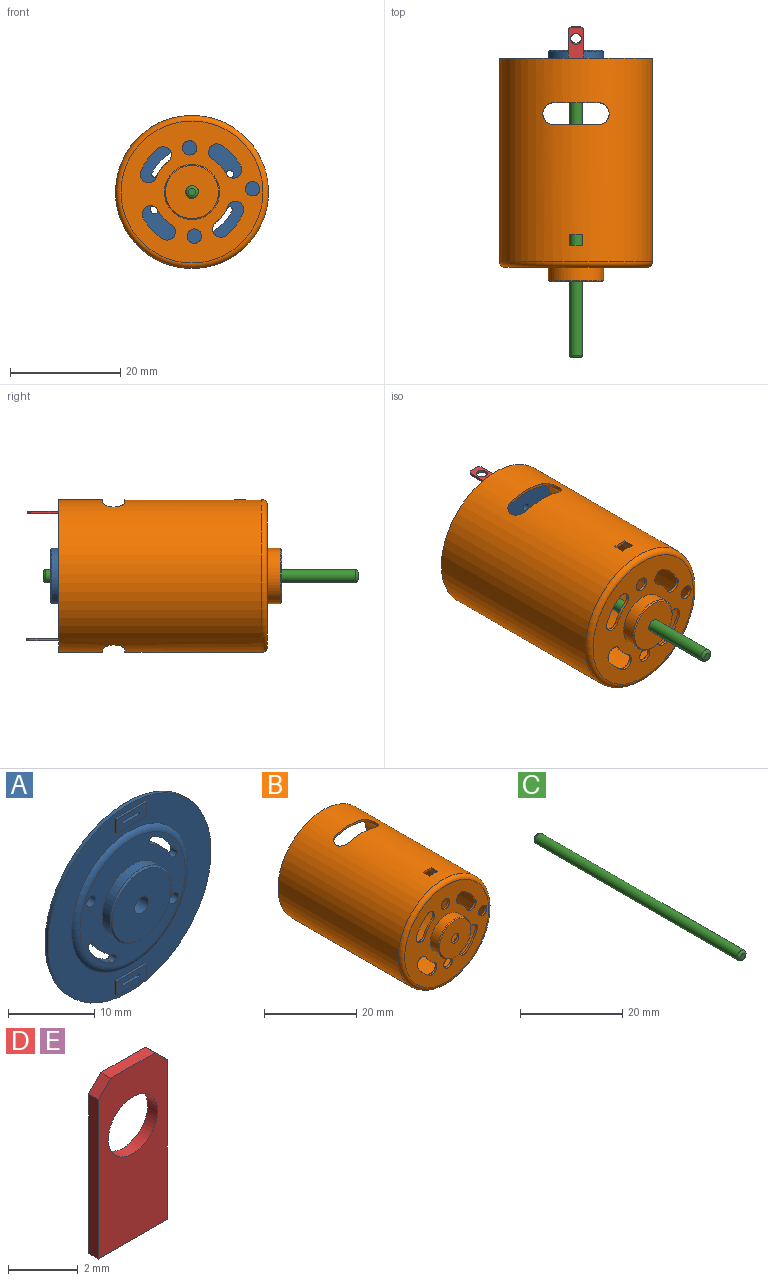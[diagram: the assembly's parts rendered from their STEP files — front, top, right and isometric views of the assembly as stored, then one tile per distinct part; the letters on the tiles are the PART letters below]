
ASSEMBLY  parts=5 mates=4
PART A: 37 faces, bbox 26.7x2.5x26.7 mm
  f0: plane 26.7x26.7mm, normal (0,-1,0), area 256.4mm2, adj f19,f25,f26,f27,f28,f30,f31,f32
  f1: plane 2.8x0.8mm, normal (0,0,-1), area 2.2mm2, adj f2,f20,f21,f29
  f2: plane 0.8x0.4mm, normal (-1,0,0), area 0.3mm2, adj f1,f3,f21,f29
  f3: plane 2.8x0.8mm, normal (0,0,1), area 2.2mm2, adj f2,f20,f21,f29
  f4: cylinder r=8mm len=3.87mm, axis (0,1,0), area 5.6mm2, adj f5,f14,f21,f22
  f5: cylinder r=0.5mm len=1mm, axis (0,1,0), area 1.6mm2, adj f4,f6,f21,f22
  f6: cylinder r=7mm len=3.39mm, axis (0,1,0), area 4.9mm2, adj f5,f14,f21,f22
  f7: cylinder r=0.5mm len=1mm, axis (0,1,0), area 1.6mm2, adj f8,f17,f21,f22
  f8: cylinder r=8mm len=3.87mm, axis (0,1,0), area 5.6mm2, adj f7,f9,f21,f22
  f9: cylinder r=0.5mm len=1mm, axis (0,1,0), area 1.6mm2, adj f8,f17,f21,f22
  f10: plane 2.8x0.8mm, normal (0,0,1), area 2.2mm2, adj f11,f18,f21,f34
  f11: plane 0.8x0.4mm, normal (1,0,0), area 0.3mm2, adj f10,f12,f21,f34
  f12: plane 2.8x0.8mm, normal (0,0,-1), area 2.2mm2, adj f11,f18,f21,f34
  f13: cylinder r=1.15mm len=2.5mm, axis (0,1,0), area 18.1mm2, adj f21,f24
  f14: cylinder r=0.5mm len=1mm, axis (0,1,0), area 1.6mm2, adj f4,f6,f21,f22
  f15: cylinder r=0.75mm len=1.5mm, axis (0,1,0), area 4.7mm2, adj f21,f22
  f16: cylinder r=0.75mm len=1.5mm, axis (0,1,0), area 4.7mm2, adj f21,f22
  f17: cylinder r=7mm len=3.39mm, axis (0,1,0), area 4.9mm2, adj f7,f9,f21,f22
  f18: plane 0.8x0.4mm, normal (-1,0,0), area 0.3mm2, adj f10,f12,f21,f34
  f19: cylinder r=13.35mm len=26.7mm, axis (0,1,0), area 41.9mm2, adj f0,f21
  f20: plane 0.8x0.4mm, normal (1,0,0), area 0.3mm2, adj f1,f3,f21,f29
  f21: plane 26.7x26.7mm, normal (0,1,0), area 537.9mm2, adj f1,f2,f3,f4,f5,f6,f7,f8
  f22: plane 17.27x17.27mm, normal (0,-1,0), area 140.1mm2, adj f4,f5,f6,f7,f8,f9,f14,f15
  f23: cylinder r=5mm len=10mm, axis (0,1,0), area 40.8mm2, adj f22,f36
  f24: plane 9.6x9.6mm, normal (0,-1,0), area 68.2mm2, adj f13,f36
  f25: plane 5x0.3mm, normal (0,0,-1), area 1.5mm2, adj f0,f26,f28,f29
  f26: plane 2x0.3mm, normal (1,0,0), area 0.6mm2, adj f0,f25,f27,f29
  f27: plane 5x0.3mm, normal (0,0,1), area 1.5mm2, adj f0,f26,f28,f29
  f28: plane 2x0.3mm, normal (-1,0,0), area 0.6mm2, adj f0,f25,f27,f29
  f29: plane 5x2mm, normal (0,-1,0), area 8.9mm2, adj f1,f2,f3,f20,f25,f26,f27,f28
  f30: plane 5x0.3mm, normal (0,0,-1), area 1.5mm2, adj f0,f31,f33,f34
  f31: plane 2x0.3mm, normal (1,0,0), area 0.6mm2, adj f0,f30,f32,f34
  f32: plane 5x0.3mm, normal (0,0,1), area 1.5mm2, adj f0,f31,f33,f34
  f33: plane 2x0.3mm, normal (-1,0,0), area 0.6mm2, adj f0,f30,f32,f34
  f34: plane 5x2mm, normal (0,-1,0), area 8.9mm2, adj f10,f11,f12,f18,f30,f31,f32,f33
  f35: torus R=8.63mm, axis (0,1,0), area 60mm2, adj f0,f22
  f36: cone r=4.8mm half-angle=45deg, axis (0,1,0), area 8.7mm2, adj f23,f24
PART B: 43 faces, bbox 30x40.4x30 mm
  f0: plane 25.7x25.7mm, normal (0,-1,0), area 342.6mm2, adj f4,f9,f10,f11,f12,f13,f14,f15
  f1: plane 26.7x26.7mm, normal (0,1,0), area 398.7mm2, adj f6,f7,f9,f10,f11,f12,f13,f14
  f2: cylinder r=13.85mm len=36.8mm, axis (0,-1,0), area 3105.7mm2, adj f3,f28,f31,f32,f33,f34,f35,f36
  f3: plane 27.7x27.7mm, normal (0,1,0), area 42.7mm2, adj f2,f6
  f4: cylinder r=5mm len=10mm, axis (0,1,0), area 75.4mm2, adj f0,f29
  f5: plane 9.6x9.6mm, normal (0,-1,0), area 68.2mm2, adj f29,f30
  f6: cylinder r=13.35mm len=37.3mm, axis (0,-1,0), area 3031.8mm2, adj f1,f3,f31,f32,f33,f34,f35,f36
  f7: cylinder r=4.5mm len=9mm, axis (0,1,0), area 73.5mm2, adj f1,f8
  f8: plane 9x9mm, normal (0,1,0), area 59.5mm2, adj f7,f30
  f9: cylinder r=1.3mm len=2.6mm, axis (0,-1,0), area 4.1mm2, adj f0,f1
  f10: cylinder r=10mm len=4.13mm, axis (0,-1,0), area 2.6mm2, adj f0,f1,f11,f13
  f11: cylinder r=1.5mm len=2.89mm, axis (0,-1,0), area 2.4mm2, adj f0,f1,f10,f12
  f12: cylinder r=7mm len=2.89mm, axis (0,-1,0), area 1.8mm2, adj f0,f1,f11,f13
  f13: cylinder r=1.5mm len=2.68mm, axis (0,-1,0), area 2.4mm2, adj f0,f1,f10,f12
  f14: cylinder r=1.3mm len=2.6mm, axis (0,-1,0), area 4.1mm2, adj f0,f1
  f15: cylinder r=10mm len=3.79mm, axis (0,-1,0), area 2.6mm2, adj f0,f1,f16,f18
  f16: cylinder r=1.5mm len=2.77mm, axis (0,-1,0), area 2.4mm2, adj f0,f1,f15,f17
  f17: cylinder r=7mm len=2.65mm, axis (0,-1,0), area 1.8mm2, adj f0,f1,f16,f18
  f18: cylinder r=1.5mm len=2.82mm, axis (0,-1,0), area 2.4mm2, adj f0,f1,f15,f17
  f19: cylinder r=1.3mm len=2.6mm, axis (0,-1,0), area 4.1mm2, adj f0,f1
  f20: cylinder r=1.5mm len=2.68mm, axis (0,-1,0), area 2.4mm2, adj f0,f1,f21,f23
  f21: cylinder r=10mm len=4.13mm, axis (0,-1,0), area 2.6mm2, adj f0,f1,f20,f22
  f22: cylinder r=1.5mm len=2.89mm, axis (0,-1,0), area 2.4mm2, adj f0,f1,f21,f23
  f23: cylinder r=7mm len=2.89mm, axis (0,-1,0), area 1.8mm2, adj f0,f1,f20,f22
  f24: cylinder r=10mm len=3.79mm, axis (0,-1,0), area 2.6mm2, adj f0,f1,f25,f27
  f25: cylinder r=1.5mm len=2.77mm, axis (0,-1,0), area 2.4mm2, adj f0,f1,f24,f26
  f26: cylinder r=7mm len=2.65mm, axis (0,-1,0), area 1.8mm2, adj f0,f1,f25,f27
  f27: cylinder r=1.5mm len=2.82mm, axis (0,-1,0), area 2.4mm2, adj f0,f1,f24,f26
  f28: torus R=12.85mm, axis (0,-1,0), area 133.1mm2, adj f0,f2
  f29: cone r=4.8mm half-angle=45deg, axis (0,1,0), area 8.7mm2, adj f4,f5
  f30: cylinder r=1.15mm len=2.3mm, axis (0,1,0), area 3.6mm2, adj f5,f8
  f31: cylinder r=2mm len=4mm, axis (0,0,1), area 3.4mm2, adj f2,f6,f32,f34
  f32: plane 8x1.11mm, normal (0,1,0), area 4.1mm2, adj f2,f6,f31,f33
  f33: cylinder r=2mm len=4mm, axis (0,0,1), area 3.4mm2, adj f2,f6,f32,f34
  f34: plane 8x1.11mm, normal (0,-1,0), area 4.1mm2, adj f2,f6,f31,f33
  f35: plane 8x1.11mm, normal (0,-1,0), area 4.1mm2, adj f2,f6,f36,f38
  f36: cylinder r=2mm len=4mm, axis (0,0,1), area 3.4mm2, adj f2,f6,f35,f37
  f37: plane 8x1.11mm, normal (0,1,0), area 4.1mm2, adj f2,f6,f36,f38
  f38: cylinder r=2mm len=4mm, axis (0,0,1), area 3.4mm2, adj f2,f6,f35,f37
  f39: plane 2.5x0.56mm, normal (0,1,0), area 1.3mm2, adj f2,f6,f40,f42
  f40: plane 2x0.5mm, normal (-1,0,0), area 1mm2, adj f2,f6,f39,f41
  f41: plane 2.5x0.56mm, normal (0,-1,0), area 1.3mm2, adj f2,f6,f40,f42
  f42: plane 2x0.5mm, normal (1,0,0), area 1mm2, adj f2,f6,f39,f41
PART C: 5 faces, bbox 2.5x57x2.5 mm
  f0: cylinder r=1.15mm len=56mm, axis (0,1,0), area 404.6mm2, adj f3,f4
  f1: plane 1.3x1.3mm, normal (0,-1,0), area 1.3mm2, adj f4
  f2: plane 1.3x1.3mm, normal (0,1,0), area 1.3mm2, adj f3
  f3: torus R=0.65mm, axis (0,-1,0), area 4.8mm2, adj f0,f2
  f4: torus R=0.65mm, axis (0,-1,0), area 4.8mm2, adj f0,f1
PART D: 9 faces, bbox 2.8x0.4x6.1 mm
  f0: plane 5.6x0.4mm, normal (1,0,0), area 2.2mm2, adj f3,f5,f6,f7
  f1: plane 1.8x0.4mm, normal (0,0,1), area 0.7mm2, adj f5,f6,f7,f8
  f2: plane 5.6x0.4mm, normal (-1,0,0), area 2.2mm2, adj f3,f5,f6,f8
  f3: plane 2.8x0.4mm, normal (0,0,-1), area 1.1mm2, adj f0,f2,f5,f6
  f4: cylinder r=1mm len=2mm, axis (0,1,0), area 2.5mm2, adj f5,f6
  f5: plane 6.1x2.8mm, normal (0,-1,0), area 13.7mm2, adj f0,f1,f2,f3,f4,f7,f8
  f6: plane 6.1x2.8mm, normal (0,1,0), area 13.7mm2, adj f0,f1,f2,f3,f4,f7,f8
  f7: plane 0.5x0.5mm, normal (0.71,0,0.71), area 0.3mm2, adj f0,f1,f5,f6
  f8: plane 0.5x0.5mm, normal (-0.71,0,0.71), area 0.3mm2, adj f1,f2,f5,f6
PART E: same geometry as D
PLACE A rot(axis=(1,0,0),180deg) t=(0,36.8,0)mm
PLACE B at identity fixed
PLACE C rot(axis=(0,-1,0),30.9deg) t=(0,40.6,0)mm
PLACE D rot(axis=(-1,0,0),90deg) t=(0,40.35,11.3)mm
PLACE E rot(axis=(-1,0,0),90deg) t=(0,40.65,-11.7)mm
MATE slider A.f19 <-> B.f2  axis (0,1,0) through (0,37.3,0)mm
MATE fastened D.f3 <-> A.f0  axis (0,-1,0) through (0,37.3,11.5)mm
MATE fastened E.f3 <-> A.f29  axis (0,-1,0) through (0,37.6,-11.5)mm
MATE revolute C.f0 <-> B.f26  axis (0,-1,0) through (0,-16.4,0)mm
